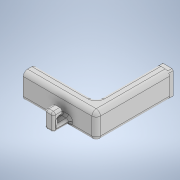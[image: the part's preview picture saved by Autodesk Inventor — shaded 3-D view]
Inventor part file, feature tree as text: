
AUTODESK INVENTOR PART (.ipt)
format: ipt  version: 2020 (Build 240168000, 168)  size: 268,288 bytes
history: native  units: in
note: dims shown in document units (in); Inventor stores cm internally (conversion verified against a paired STEP export)
features: sketch x6, extrude x4, hole x2, fillet x2
ambient origin geometry x8: Origin, YZ Plane, XZ Plane, XY Plane, X Axis, Y Axis, Z Axis, Center Point
bodies: Solid1 (feature_tree)
feature tree (14):
  extrude  "Extrusion1"  Depth=2.263in
  hole  "Hole1"  [1 undecoded]
  hole  "Hole2"  [1 undecoded]
  extrude  "Extrusion2"  Depth=0.125in
  fillet  "Fillet1"  Radius=0.1875in
  extrude  "Extrusion3"  Depth=0.0625in
  extrude  "Extrusion4"  Depth=0.0625in
  fillet  "Fillet2"  Radius=0.02in
  sketch  "Sketch1"  dims[d0=0.375in d1=2.263in]
  sketch  "Sketch2"  dims[d2=1.7475in d3=0.375in]
  sketch  "Sketch3"  dims[d4=0.75in d5=0.0in d6=0.1875in]
  sketch  "Sketch4"  dims[d7=0.125in d8=0.5in]
  sketch  "Sketch5"  dims[d9=0.1562in d10=0.75in d11=0.225in d12=0.25in d13=0.5635in d14=0.5in d15=0.8108in d16=0.1875in]
  sketch  "Sketch6"  dims[d17=0.375in d18=0.185in d19=0.37in d20=0.1562in d21=0.75in d22=0.225in d23=0.25in d24=0.5635in d25=0.5in d26=0.8108in d27=0.02in d28=0.02in d29=0.02in d30=0.02in d31=0.13in d32=0.0in d33=0.125in d34=0.749in d35=0.125in d36=0.0in d37=0.25in d38=90.0deg d39=0.5in d40=0.0in d41=0.2in d42=135.0deg d43=0.5in d44=0.0in d45=0.0625in]
note: 2 required parameter values undecoded (feature->parameter linkage not recoverable at this tier; creation-order binding heuristic only, values carry confidence <= 0.55)
